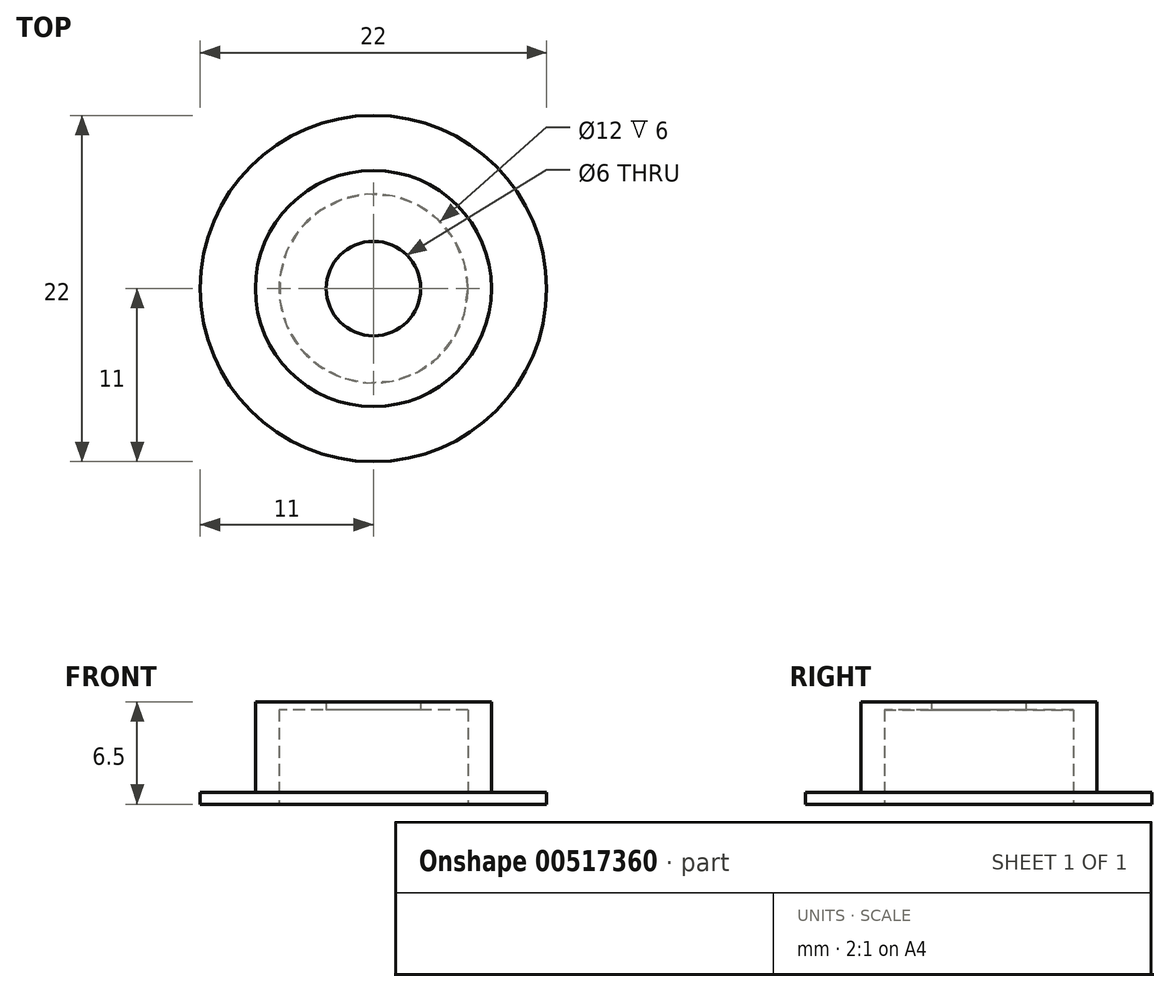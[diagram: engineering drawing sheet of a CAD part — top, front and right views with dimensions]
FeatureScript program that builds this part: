
annotation { "Feature Type Name" : "Feature", "Feature Type Description" : "" }
export const myFeature = defineFeature(function(context is Context, id is Id, definition is map)
    precondition{}
    {
        {
            var Q0;
            Q0=qCreatedBy(makeId("Top.planeOp"),FACE);
            var sketch = newSketch(context, id + "F0", { "sketchPlane" : qUnion([Q0])});
            skCircle(sketch, "E0", {"center": v(0, 0) * mm, "radius": 6 * mm});
            skCircle(sketch, "E1.0", {"center": v(0, 0) * mm, "radius": 7.5 * mm});
            skSolve(sketch);
        }
        {
            var Q0;
            Q0 = qSketchRegion(id + "F0", true);
            extrude(context, id + "F1", {"entities" : qUnion([Q0]), "depth" : 6 * mm, "offsetDistance" : 25 * mm});
        }
        {
            var Q0;
            Q0=makeQuery(id+"F1.opExtrude","CAP_FACE",FACE,{"disambiguationData":[OSD([sQuery(id+"F0.wireOp",EDGE,"E0"),sQuery(id+"F0.wireOp",EDGE,"E1.0")])],"isStart":false});
            var sketch = newSketch(context, id + "F2", { "sketchPlane" : qUnion([Q0])});
            skCircle(sketch, "E2", {"center": v(0, 0) * mm, "radius": 7.5 * mm});
            skCircle(sketch, "E3", {"center": v(0, 0) * mm, "radius": 3 * mm});
            skSolve(sketch);
        }
        {
            var Q0;
            Q0 = qSketchRegion(id + "F2", true);
            extrude(context, id + "F3", {"entities" : qUnion([Q0]), "operationType" : NewBodyOperationType.ADD, "depth" : .5 * mm, "offsetDistance" : 25 * mm});
        }
        {
            var Q0;
            Q0=qCreatedBy(makeId("Top.planeOp"),FACE);
            var sketch = newSketch(context, id + "F4", { "sketchPlane" : qUnion([Q0])});
            skCircle(sketch, "E4", {"center": v(0, 0) * mm, "radius": 6 * mm});
            skCircle(sketch, "E5.0", {"center": v(0, 0) * mm, "radius": 11 * mm});
            skSolve(sketch);
        }
        {
            var Q0;
            Q0 = qSketchRegion(id + "F4", true);
            extrude(context, id + "F5", {"entities" : qUnion([Q0]), "operationType" : NewBodyOperationType.ADD, "depth" : .75 * mm, "offsetDistance" : 25 * mm});
        }
    });
